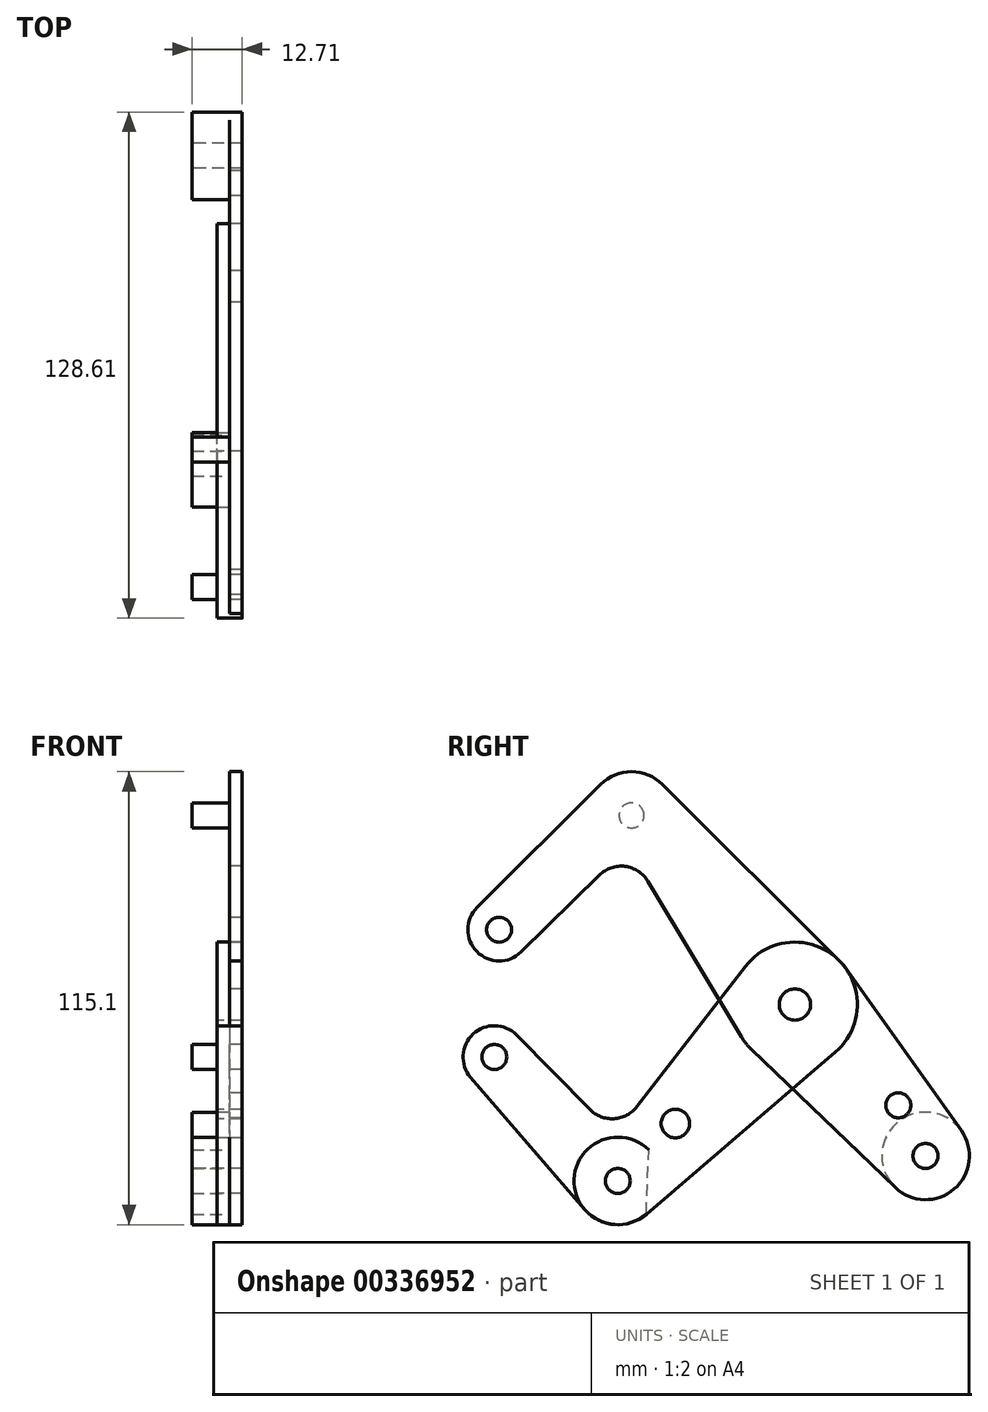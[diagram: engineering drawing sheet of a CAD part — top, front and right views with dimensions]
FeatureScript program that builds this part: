
annotation { "Feature Type Name" : "Feature", "Feature Type Description" : "" }
export const myFeature = defineFeature(function(context is Context, id is Id, definition is map)
    precondition{}
    {
        {
            var Q0;
            Q0=qCreatedBy(makeId("Right.planeOp"),FACE);
            var sketch = newSketch(context, id + "F0", { "sketchPlane" : qUnion([Q0])});
            skCircle(sketch, "E0", {"center": v(-75.14, 19.02) * mm, "radius": 7.94 * mm});
            skCircle(sketch, "E1", {"center": v(-41.5, 48.07) * mm, "radius": 11.11 * mm});
            skCircle(sketch, "E2", {"center": v(0, 0) * mm, "radius": 15.88 * mm});
            skCircle(sketch, "E3", {"center": v(33.2, -38.45) * mm, "radius": 11.11 * mm});
            skCircle(sketch, "E4", {"center": v(0, 0) * mm, "radius": 3.98 * mm});
            skLineSegment(sketch, "E5", {"start": v(-75.14, 19.02) * mm, "end": v(-41.5, 48.07) * mm});
            skLineSegment(sketch, "E6", {"start": v(-41.5, 48.07) * mm, "end": v(0, 0) * mm});
            skLineSegment(sketch, "E7", {"start": v(33.2, -38.45) * mm, "end": v(0, 0) * mm});
            skCircle(sketch, "E8", {"center": v(33.2, -38.45) * mm, "radius": 3.18 * mm});
            skCircle(sketch, "E9", {"center": v(26.27, -25.57) * mm, "radius": 3.18 * mm});
            skLineSegment(sketch, "E10", {"start": v(0, 0) * mm, "end": v(23.87, -27.65) * mm});
            skCircle(sketch, "E11", {"center": v(-75.14, 19.02) * mm, "radius": 3.18 * mm});
            skCircle(sketch, "E12", {"center": v(-41.5, 48.07) * mm, "radius": 3.18 * mm});
            skCircle(sketch, "E13", {"center": v(0, 0) * mm, "radius": 3.18 * mm});
            skPoint(sketch, "E14", {"position": v(-49.34, 55.94) * mm});
            skPoint(sketch, "E15", {"position": v(-33.65, 55.94) * mm});
            skPoint(sketch, "E16", {"position": v(-69.58, 13.36) * mm});
            skPoint(sketch, "E17", {"position": v(-80.74, 24.65) * mm});
            skPoint(sketch, "E18", {"position": v(-13.61, -8.17) * mm});
            skPoint(sketch, "E19", {"position": v(-11, -11.45) * mm});
            skPoint(sketch, "E20", {"position": v(11.2, 11.25) * mm});
            skPoint(sketch, "E21", {"position": v(12.94, 9.2) * mm});
            skLineSegment(sketch, "E22", {"start": v(-80.74, 24.65) * mm, "end": v(-49.34, 55.94) * mm});
            skLineSegment(sketch, "E23", {"start": v(-33.65, 55.94) * mm, "end": v(11.2, 11.25) * mm});
            skPoint(sketch, "E24", {"position": v(42.25, -32.01) * mm});
            skPoint(sketch, "E25", {"position": v(25.5, -46.47) * mm});
            skLineSegment(sketch, "E26", {"start": v(12.94, 9.2) * mm, "end": v(42.25, -32.01) * mm});
            skLineSegment(sketch, "E27", {"start": v(25.5, -46.47) * mm, "end": v(-11, -11.45) * mm});
            skArc(sketch, "E28", {"start": v(-37.32, 31.32) * mm, "mid": v(-43.13, 35.1) * mm, "end": v(-49.7, 32.9) * mm});
            skLineSegment(sketch, "E29", {"start": v(-49.7, 32.9) * mm, "end": v(-69.58, 13.36) * mm});
            skLineSegment(sketch, "E30", {"start": v(-37.32, 31.32) * mm, "end": v(-13.61, -8.17) * mm});
            skSolve(sketch);
        }
        {
            var Q0;
            Q0=qCreatedBy(makeId("Right.planeOp"),FACE);
            var sketch = newSketch(context, id + "F1", { "sketchPlane" : qUnion([Q0])});
            skCircle(sketch, "E31", {"center": v(-76.36, -13.31) * mm, "radius": 7.94 * mm});
            skCircle(sketch, "E32", {"center": v(-76.36, -13.31) * mm, "radius": 3.18 * mm});
            skCircle(sketch, "E33", {"center": v(-45, -44.8) * mm, "radius": 11.11 * mm});
            skCircle(sketch, "E34", {"center": v(-45, -44.8) * mm, "radius": 3.18 * mm});
            skCircle(sketch, "E35", {"center": v(-30.36, -30.24) * mm, "radius": 3.61 * mm});
            skLineSegment(sketch, "E36", {"start": v(-76.36, -13.31) * mm, "end": v(-45, -44.8) * mm, "construction": true});
            skLineSegment(sketch, "E37", {"start": v(-30.36, -30.24) * mm, "end": v(-45, -44.8) * mm, "construction": true});
            skCircle(sketch, "E38", {"center": v(0, 0) * mm, "radius": 15.88 * mm});
            skLineSegment(sketch, "E39", {"start": v(-30.36, -30.24) * mm, "end": v(0, 0) * mm, "construction": true});
            skCircle(sketch, "E40", {"center": v(0, 0) * mm, "radius": 3.98 * mm});
            skCircle(sketch, "E41", {"center": v(0, 0) * mm, "radius": 3.18 * mm});
            skPoint(sketch, "E42", {"position": v(-70.7, -7.74) * mm});
            skPoint(sketch, "E43", {"position": v(-82.37, -18.5) * mm});
            skPoint(sketch, "E44", {"position": v(-53.4, -52.07) * mm});
            skPoint(sketch, "E45", {"position": v(-37.77, -53.25) * mm});
            skPoint(sketch, "E46", {"position": v(-12.56, 9.71) * mm});
            skPoint(sketch, "E47", {"position": v(10.33, -12.06) * mm});
            skLineSegment(sketch, "E48", {"start": v(-82.37, -18.5) * mm, "end": v(-53.4, -52.07) * mm});
            skLineSegment(sketch, "E49", {"start": v(-37.77, -53.25) * mm, "end": v(10.33, -12.06) * mm});
            skPoint(sketch, "E50", {"position": v(-52.08, -26.64) * mm});
            skPoint(sketch, "E51", {"position": v(-40.13, -25.93) * mm});
            skLineSegment(sketch, "E52", {"start": v(-70.7, -7.74) * mm, "end": v(-52.08, -26.64) * mm});
            skLineSegment(sketch, "E53", {"start": v(-40.13, -25.93) * mm, "end": v(-12.56, 9.71) * mm});
            skArc(sketch, "E54", {"start": v(-52.08, -26.64) * mm, "mid": v(-45.94, -29) * mm, "end": v(-40.13, -25.93) * mm});
            skLineSegment(sketch, "E55", {"start": v(-46.42, -21.06) * mm, "end": v(-45, -44.8) * mm, "construction": true});
            skPoint(sketch, "E56", {"position": v(-45.83, -30.85) * mm});
            skLineSegment(sketch, "E57", {"start": v(-52.08, -26.64) * mm, "end": v(-45.83, -30.85) * mm, "construction": true});
            skLineSegment(sketch, "E58", {"start": v(-45.83, -30.85) * mm, "end": v(-40.13, -25.93) * mm, "construction": true});
            skLineSegment(sketch, "E59", {"start": v(-37.12, -36.97) * mm, "end": v(-37.77, -53.25) * mm});
            skSolve(sketch);
        }
        {
            var Q0;
            Q0 = qSketchRegion(id + "F0", true);
            var Q1;
            Q1 = qSketchRegion(id + "F1", true);
            var Q2;
            {var subQ0=sQuery(id+"F0.wireOp",EDGE,"E5");var subQ1=sQuery(id+"F0.wireOp",EDGE,"E1");var subQ2=makeQuery(id+"F0.imprint","INTERSECT",VERTEX,{"derivedFrom":[subQ1,subQ0]});Q2=makeQuery(id+"F0.imprint","IMPRINT",FACE,{"disambiguationData":[TD([[makeQuery(id+"F0.imprint","IMPRINT",EDGE,{"disambiguationData":[TD([[subQ2,-1.0]])],"derivedFrom":subQ1}),1.0]])]});}
            var Q3;
            {var subQ0=sQuery(id+"F1.wireOp",EDGE,"E36");var subQ1=sQuery(id+"F1.wireOp",EDGE,"E33");var subQ2=makeQuery(id+"F1.imprint","INTERSECT",VERTEX,{"derivedFrom":[subQ1,subQ0]});Q3=makeQuery(id+"F1.imprint","IMPRINT",FACE,{"disambiguationData":[TD([[makeQuery(id+"F1.imprint","IMPRINT",EDGE,{"disambiguationData":[TD([[subQ2,1.0]])],"derivedFrom":subQ1}),1.0]])]});}
            extrude(context, id + "F2", {"entities" : qUnion([Q0, Q1, Q2, Q3]), "depth" : 3.17 * mm});
        }
        {
            var Q0;
            Q0 = qSketchRegion(id + "F1", true);
            var Q1;
            {var subQ0=sQuery(id+"F1.wireOp",EDGE,"E36");var subQ1=sQuery(id+"F1.wireOp",EDGE,"E33");var subQ2=makeQuery(id+"F1.imprint","INTERSECT",VERTEX,{"derivedFrom":[subQ1,subQ0]});Q1=makeQuery(id+"F1.imprint","IMPRINT",FACE,{"disambiguationData":[TD([[makeQuery(id+"F1.imprint","IMPRINT",EDGE,{"disambiguationData":[TD([[subQ2,1.0]])],"derivedFrom":subQ1}),1.0]])]});}
            extrude(context, id + "F3", {"entities" : qUnion([Q0, Q1]), "oppositeDirection" : true, "depth" : 3.17 * mm});
        }
        {
            var Q0;
            Q0=makeQuery(id+"F2.opExtrude","CAP_FACE",FACE,{"disambiguationData":[OSD([sQuery(id+"F0.wireOp",EDGE,"E0"),sQuery(id+"F0.wireOp",EDGE,"E1"),sQuery(id+"F0.wireOp",EDGE,"E2"),sQuery(id+"F0.wireOp",EDGE,"E3"),sQuery(id+"F0.wireOp",EDGE,"E4"),sQuery(id+"F0.wireOp",EDGE,"E8"),sQuery(id+"F0.wireOp",EDGE,"E9"),sQuery(id+"F0.wireOp",EDGE,"E11"),sQuery(id+"F0.wireOp",EDGE,"E12"),sQuery(id+"F0.wireOp",EDGE,"E22"),sQuery(id+"F0.wireOp",EDGE,"E23"),sQuery(id+"F0.wireOp",EDGE,"E26"),sQuery(id+"F0.wireOp",EDGE,"E27"),sQuery(id+"F0.wireOp",EDGE,"E28"),sQuery(id+"F0.wireOp",EDGE,"E29"),sQuery(id+"F0.wireOp",EDGE,"E30")])],"isStart":false});
            var sketch = newSketch(context, id + "F4", { "sketchPlane" : qUnion([Q0])});
            skCircle(sketch, "E60", {"center": v(-41.5, 48.07) * mm, "radius": 3.98 * mm});
            skCircle(sketch, "E61", {"center": v(33.2, -38.45) * mm, "radius": 11.11 * mm});
            skCircle(sketch, "E62", {"center": v(0, 0) * mm, "radius": 3.98 * mm});
            skSolve(sketch);
        }
        {
            var Q0;
            Q0=qCreatedBy(makeId("Right.planeOp"),FACE);
            cPlane(context, id + "F5", {"entities" : qUnion([Q0]), "cplaneType" : CPlaneType.OFFSET, "offset" : 9.52 * mm, "oppositeDirection" : true, "width" : 152.4 * mm, "height" : 152.4 * mm});
        }
        {
            var Q0;
            Q0=makeQuery(id+"F0.imprint","IMPRINT",FACE,{"disambiguationData":[TD([[makeQuery(id+"F0.imprint","IMPRINT",EDGE,{"derivedFrom":sQuery(id+"F0.wireOp",EDGE,"E8")}),-1.0]])]});
            var Q1;
            Q1=makeQuery(id+"F4.imprint","IMPRINT",FACE,{"disambiguationData":[TD([[makeQuery(id+"F4.imprint","IMPRINT",EDGE,{"derivedFrom":makeQuery(id+"F2.opExtrude","CAP_EDGE",EDGE,{"disambiguationData":[OSD([sQuery(id+"F0.wireOp",EDGE,"E12")])],"isStart":false})}),1.0]])]});
            var Q2;
            Q2=makeQuery(id+"F1.imprint","IMPRINT",FACE,{"disambiguationData":[TD([[makeQuery(id+"F1.imprint","IMPRINT",EDGE,{"derivedFrom":sQuery(id+"F1.wireOp",EDGE,"E32")}),1.0]])]});
            var Q3;
            Q3=qCreatedBy(id+"F5.planeOp",FACE);
            extrude(context, id + "F6", {"entities" : qUnion([Q0, Q1, Q2]), "operationType" : NewBodyOperationType.ADD, "endBound" : BoundingType.UP_TO_SURFACE, "oppositeDirection" : true, "endBoundEntityFace" : qUnion([Q3]), "depth" : 25.4 * mm});
        }
        {
            var Q0;
            Q0=makeQuery(id+"F1.imprint","IMPRINT",FACE,{"disambiguationData":[TD([[makeQuery(id+"F1.imprint","IMPRINT",EDGE,{"derivedFrom":sQuery(id+"F1.wireOp",EDGE,"E34")}),-1.0]])]});
            var Q1;
            Q1=qCreatedBy(id+"F5.planeOp",FACE);
            extrude(context, id + "F7", {"entities" : qUnion([Q0]), "endBound" : BoundingType.UP_TO_SURFACE, "oppositeDirection" : true, "endBoundEntityFace" : qUnion([Q1]), "depth" : 25.4 * mm});
        }
    });
